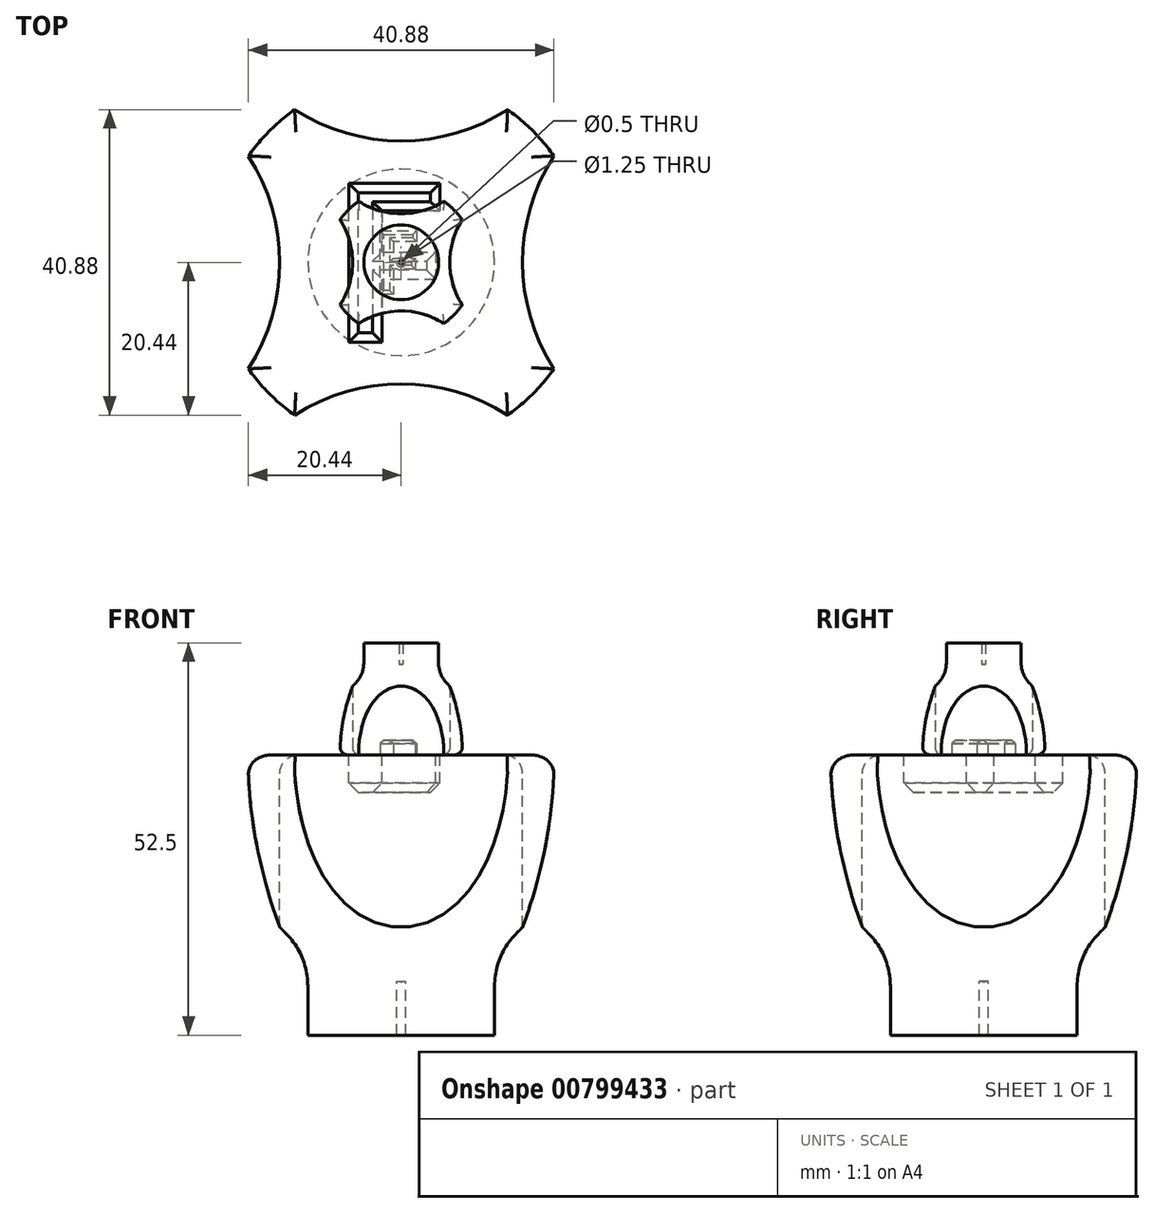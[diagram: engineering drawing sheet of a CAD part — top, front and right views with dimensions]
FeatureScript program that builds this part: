
annotation { "Feature Type Name" : "Feature", "Feature Type Description" : "" }
export const myFeature = defineFeature(function(context is Context, id is Id, definition is map)
    precondition{}
    {
        {
            var Q0;
            Q0=qCreatedBy(makeId("Top.planeOp"),FACE);
            var sketch = newSketch(context, id + "F0", { "sketchPlane" : qUnion([Q0])});
            skCircle(sketch, "E0", {"center": v(0, 0) * mm, "radius": 10 * mm});
            skCircle(sketch, "E1", {"center": v(0, 17) * mm, "radius": 10.5 * mm});
            skCircle(sketch, "E2.1.0", {"center": v(-17, 0) * mm, "radius": 10.5 * mm});
            skCircle(sketch, "E2.2.0", {"center": v(0, -17) * mm, "radius": 10.5 * mm});
            skCircle(sketch, "E2.3.0", {"center": v(17, 0) * mm, "radius": 10.5 * mm});
            skSolve(sketch);
        }
        {
            var Q0;
            Q0=qCreatedBy(makeId("Front.planeOp"),FACE);
            var Q1;
            Q1=qCreatedBy(makeId("Front.planeOp"),FACE);
            var sketch = newSketch(context, id + "F1", { "sketchPlane" : qUnion([Q0, Q1])});
            skLineSegment(sketch, "E3.0", {"start": v(-10, 0) * mm, "end": v(0, 0) * mm});
            skEllipticalArc(sketch, "E4", {});
            skLineSegment(sketch, "E5", {"start": v(0, -5.12) * mm, "end": v(0, 66.05) * mm, "construction": true});
            skLineSegment(sketch, "E6", {"start": v(0, 0) * mm, "end": v(0, 12.13) * mm});
            skPoint(sketch, "E7.orphan", {"position": v(10, 0) * mm});
            const initialGuessF1  = {"E4": [0, 0, -1, 0, 0.01, 0.012128176619593395, 4.71238898038469, 6.283185307179586]};
            skSetInitialGuess(sketch, initialGuessF1);
            skSolve(sketch);
        }
        {
            var Q0;
            Q0=makeQuery(id+"F1.imprint","IMPRINT",FACE,{"disambiguationData":[TD([[makeQuery(id+"F1.imprint","IMPRINT",EDGE,{"derivedFrom":sQuery(id+"F1.wireOp",EDGE,"E4")}),1.0]])]});
            var Q1;
            Q1=sQuery(id+"F1.wireOp",EDGE,"E5");
            revolve(context, id + "F2", {"surfaceOperationType" : NewSurfaceOperationType.NEW, "entities" : qUnion([Q0]), "axis" : qUnion([Q1]), "revolveType" : RevolveType.FULL});
        }
        {
            var Q0;
            {var subQ0=sQuery(id+"F0.wireOp",EDGE,"E2.1.0");var subQ1=sQuery(id+"F0.wireOp",EDGE,"E0");var subQ2=makeQuery(id+"F0.imprint","INTERSECT",VERTEX,{"disambiguationData":[OD(0.0)],"derivedFrom":[subQ1,subQ0]});Q0=makeQuery(id+"F0.imprint","IMPRINT",FACE,{"disambiguationData":[TD([[makeQuery(id+"F0.imprint","IMPRINT",EDGE,{"disambiguationData":[TD([[subQ2,-1.0]])],"derivedFrom":subQ1}),1.0]])]});}
            var Q1;
            {var subQ0=sQuery(id+"F0.wireOp",EDGE,"E2.2.0");var subQ1=sQuery(id+"F0.wireOp",EDGE,"E0");var subQ2=makeQuery(id+"F0.imprint","INTERSECT",VERTEX,{"disambiguationData":[OD(0.0)],"derivedFrom":[subQ1,subQ0]});Q1=makeQuery(id+"F0.imprint","IMPRINT",FACE,{"disambiguationData":[TD([[makeQuery(id+"F0.imprint","IMPRINT",EDGE,{"disambiguationData":[TD([[subQ2,-1.0]])],"derivedFrom":subQ1}),1.0]])]});}
            var Q2;
            {var subQ0=sQuery(id+"F0.wireOp",EDGE,"E2.3.0");var subQ1=sQuery(id+"F0.wireOp",EDGE,"E0");var subQ2=makeQuery(id+"F0.imprint","INTERSECT",VERTEX,{"disambiguationData":[OD(0.0)],"derivedFrom":[subQ1,subQ0]});Q2=makeQuery(id+"F0.imprint","IMPRINT",FACE,{"disambiguationData":[TD([[makeQuery(id+"F0.imprint","IMPRINT",EDGE,{"disambiguationData":[TD([[subQ2,1.0]])],"derivedFrom":subQ1}),1.0]])]});}
            var Q3;
            {var subQ0=sQuery(id+"F0.wireOp",EDGE,"E1");var subQ1=sQuery(id+"F0.wireOp",EDGE,"E0");var subQ2=makeQuery(id+"F0.imprint","INTERSECT",VERTEX,{"disambiguationData":[OD(0.0)],"derivedFrom":[subQ1,subQ0]});Q3=makeQuery(id+"F0.imprint","IMPRINT",FACE,{"disambiguationData":[TD([[makeQuery(id+"F0.imprint","IMPRINT",EDGE,{"disambiguationData":[TD([[subQ2,-1.0]])],"derivedFrom":subQ1}),1.0]])]});}
            var Q4;
            Q4=makeQuery(id+"F2.opRevolve","SWEPT_FACE",FACE,{"disambiguationData":[OSD([sQuery(id+"F1.wireOp",EDGE,"E4")])]});
            extrude(context, id + "F3", {"entities" : qUnion([Q0, Q1, Q2, Q3]), "operationType" : NewBodyOperationType.REMOVE, "endBound" : BoundingType.UP_TO_SURFACE, "depth" : 25 * mm, "endBoundEntityFace" : qUnion([Q4]), "offsetDistance" : 25 * mm});
        }
        {
            var Q0;
            Q0=qCreatedBy(makeId("Top.planeOp"),FACE);
            var sketch = newSketch(context, id + "F4", { "sketchPlane" : qUnion([Q0])});
            skCircle(sketch, "E8.cCircle", {"center": v(0, 0) * mm, "radius": 4 * mm, "construction": true});
            skLineSegment(sketch, "E8.0", {"start": v(2.3, -4) * mm, "end": v(-2.3, -4) * mm});
            skLineSegment(sketch, "E8.1", {"start": v(-2.3, -4) * mm, "end": v(-4.62, 0) * mm});
            skLineSegment(sketch, "E8.2", {"start": v(-4.62, 0) * mm, "end": v(-2.3, 4) * mm});
            skLineSegment(sketch, "E8.3", {"start": v(-2.3, 4) * mm, "end": v(2.3, 4) * mm});
            skLineSegment(sketch, "E8.4", {"start": v(2.3, 4) * mm, "end": v(4.62, 0) * mm});
            skLineSegment(sketch, "E8.5", {"start": v(4.62, 0) * mm, "end": v(2.3, -4) * mm});
            skPoint(sketch, "E8.0.midPoint", {"position": v(0, -4) * mm});
            skSolve(sketch);
        }
        {
            var Q0;
            Q0=makeQuery(id+"F3.boolean.opBoolean","COPY",EDGE,{"derivedFrom":makeQuery(id+"F3.opExtrude","CAP_EDGE",EDGE,{"disambiguationData":[OSD([sQuery(id+"F0.wireOp",EDGE,"E2.2.0")])],"isStart":false})});
            var Q1;
            Q1=makeQuery(id+"F3.boolean.opBoolean","COPY",EDGE,{"derivedFrom":makeQuery(id+"F3.opExtrude","CAP_EDGE",EDGE,{"disambiguationData":[OSD([sQuery(id+"F0.wireOp",EDGE,"E2.1.0")])],"isStart":false})});
            var Q2;
            Q2=makeQuery(id+"F2.opRevolve","SWEPT_FACE",FACE,{"disambiguationData":[OSD([sQuery(id+"F1.wireOp",EDGE,"E3.0")])]});
            var Q3;
            Q3=makeQuery(id+"F3.boolean.opBoolean","COPY",EDGE,{"derivedFrom":makeQuery(id+"F3.opExtrude","CAP_EDGE",EDGE,{"disambiguationData":[OSD([sQuery(id+"F0.wireOp",EDGE,"E1")])],"isStart":false})});
            var Q4;
            Q4=makeQuery(id+"F3.boolean.opBoolean","COPY",EDGE,{"derivedFrom":makeQuery(id+"F3.opExtrude","CAP_EDGE",EDGE,{"disambiguationData":[OSD([sQuery(id+"F0.wireOp",EDGE,"E2.3.0")])],"isStart":false})});
            fillet(context, id + "F5", {"entities" : qUnion([Q0, Q1, Q2, Q3, Q4]), "radius" : 1 * mm, "tangentPropagation" : true, "allowEdgeOverflow" : false});
        }
        {
            var Q0;
            Q0=qCreatedBy(makeId("Top.planeOp"),FACE);
            var sketch = newSketch(context, id + "F6", { "sketchPlane" : qUnion([Q0])});
            skCircle(sketch, "E9", {"center": v(0, 0) * mm, "radius": 5 * mm});
            skCircle(sketch, "E10", {"center": v(0, 0) * mm, "radius": 0.25 * mm});
            skSolve(sketch);
        }
        {
            var Q0;
            Q0=makeQuery(id+"F6.imprint","IMPRINT",FACE,{"disambiguationData":[TD([[makeQuery(id+"F6.imprint","IMPRINT",EDGE,{"derivedFrom":sQuery(id+"F6.wireOp",EDGE,"E9")}),1.0]])]});
            extrude(context, id + "F7", {"entities" : qUnion([Q0]), "operationType" : NewBodyOperationType.ADD, "depth" : 15 * mm, "offsetDistance" : 25 * mm});
        }
        {
            var Q0;
            Q0=makeQuery(id+"F7.boolean.opBoolean","INTERSECT",EDGE,{"derivedFrom":[makeQuery(id+"F2.opRevolve","SWEPT_FACE",FACE,{"disambiguationData":[OSD([sQuery(id+"F1.wireOp",EDGE,"E4")])]}),makeQuery(id+"F7.opExtrude","SWEPT_FACE",FACE,{"disambiguationData":[OSD([sQuery(id+"F6.wireOp",EDGE,"E9")])]})]});
            fillet(context, id + "F8", {"entities" : qUnion([Q0]), "radius" : 4 * mm, "tangentPropagation" : true, "allowEdgeOverflow" : false});
        }
        {
            var Q0;
            Q0=qCreatedBy(makeId("Top.planeOp"),FACE);
            var sketch = newSketch(context, id + "F9", { "sketchPlane" : qUnion([Q0])});
            skText(sketch, "E11", { "text": "F", "fontName": "OpenSans-Bold.ttf"});
            const initialGuessF9  = {"E11": [-0.00387, -0.00427, 1, 0, 0.00857]};
            skSetInitialGuess(sketch, initialGuessF9);
            skSolve(sketch);
        }
        {
            var Q0;
            Q0=makeQuery(id+"F9.imprint","IMPRINT",FACE,{"disambiguationData":[TD([[makeQuery(id+"F9.imprint","IMPRINT",EDGE,{"derivedFrom":sQuery(id+"F9.wireOp",EDGE,"E11.sketch_text.stroke-0")}),-1.0]])]});
            extrude(context, id + "F10", {"entities" : qUnion([Q0]), "operationType" : NewBodyOperationType.REMOVE, "depth" : 2 * mm, "offsetDistance" : 25 * mm});
        }
        {
            var Q0;
            Q0=makeQuery(id+"F10.boolean.opBoolean","COPY",FACE,{"derivedFrom":makeQuery(id+"F10.opExtrude","CAP_FACE",FACE,{"disambiguationData":[OSD([sQuery(id+"F9.wireOp",EDGE,"E11.sketch_text.stroke-0"),sQuery(id+"F9.wireOp",EDGE,"E11.sketch_text.stroke-1"),sQuery(id+"F9.wireOp",EDGE,"E11.sketch_text.stroke-2"),sQuery(id+"F9.wireOp",EDGE,"E11.sketch_text.stroke-3"),sQuery(id+"F9.wireOp",EDGE,"E11.sketch_text.stroke-4"),sQuery(id+"F9.wireOp",EDGE,"E11.sketch_text.stroke-5"),sQuery(id+"F9.wireOp",EDGE,"E11.sketch_text.stroke-6"),sQuery(id+"F9.wireOp",EDGE,"E11.sketch_text.stroke-7"),sQuery(id+"F9.wireOp",EDGE,"E11.sketch_text.stroke-8"),sQuery(id+"F9.wireOp",EDGE,"E11.sketch_text.stroke-9")])],"isStart":false})});
            var Q1;
            Q1=makeQuery(id+"F10.boolean.opBoolean","COPY",EDGE,{"derivedFrom":makeQuery(id+"F10.opExtrude","CAP_EDGE",EDGE,{"disambiguationData":[OSD([sQuery(id+"F9.wireOp",EDGE,"E11.sketch_text.stroke-9")])],"isStart":true})});
            var Q2;
            Q2=makeQuery(id+"F10.boolean.opBoolean","COPY",EDGE,{"derivedFrom":makeQuery(id+"F10.opExtrude","CAP_EDGE",EDGE,{"disambiguationData":[OSD([sQuery(id+"F9.wireOp",EDGE,"E11.sketch_text.stroke-8")])],"isStart":true})});
            var Q3;
            Q3=makeQuery(id+"F10.boolean.opBoolean","COPY",EDGE,{"derivedFrom":makeQuery(id+"F10.opExtrude","CAP_EDGE",EDGE,{"disambiguationData":[OSD([sQuery(id+"F9.wireOp",EDGE,"E11.sketch_text.stroke-7")])],"isStart":true})});
            var Q4;
            Q4=makeQuery(id+"F10.boolean.opBoolean","COPY",EDGE,{"derivedFrom":makeQuery(id+"F10.opExtrude","CAP_EDGE",EDGE,{"disambiguationData":[OSD([sQuery(id+"F9.wireOp",EDGE,"E11.sketch_text.stroke-6")])],"isStart":true})});
            var Q5;
            Q5=makeQuery(id+"F10.boolean.opBoolean","COPY",EDGE,{"derivedFrom":makeQuery(id+"F10.opExtrude","CAP_EDGE",EDGE,{"disambiguationData":[OSD([sQuery(id+"F9.wireOp",EDGE,"E11.sketch_text.stroke-5")])],"isStart":true})});
            var Q6;
            Q6=makeQuery(id+"F10.boolean.opBoolean","COPY",EDGE,{"derivedFrom":makeQuery(id+"F10.opExtrude","CAP_EDGE",EDGE,{"disambiguationData":[OSD([sQuery(id+"F9.wireOp",EDGE,"E11.sketch_text.stroke-4")])],"isStart":true})});
            var Q7;
            Q7=makeQuery(id+"F10.boolean.opBoolean","COPY",EDGE,{"derivedFrom":makeQuery(id+"F10.opExtrude","CAP_EDGE",EDGE,{"disambiguationData":[OSD([sQuery(id+"F9.wireOp",EDGE,"E11.sketch_text.stroke-3")])],"isStart":true})});
            var Q8;
            Q8=makeQuery(id+"F10.boolean.opBoolean","COPY",EDGE,{"derivedFrom":makeQuery(id+"F10.opExtrude","CAP_EDGE",EDGE,{"disambiguationData":[OSD([sQuery(id+"F9.wireOp",EDGE,"E11.sketch_text.stroke-2")])],"isStart":true})});
            var Q9;
            Q9=makeQuery(id+"F10.boolean.opBoolean","COPY",EDGE,{"derivedFrom":makeQuery(id+"F10.opExtrude","CAP_EDGE",EDGE,{"disambiguationData":[OSD([sQuery(id+"F9.wireOp",EDGE,"E11.sketch_text.stroke-1")])],"isStart":true})});
            var Q10;
            Q10=makeQuery(id+"F10.boolean.opBoolean","COPY",EDGE,{"derivedFrom":makeQuery(id+"F10.opExtrude","CAP_EDGE",EDGE,{"disambiguationData":[OSD([sQuery(id+"F9.wireOp",EDGE,"E11.sketch_text.stroke-0")])],"isStart":true})});
            chamfer(context, id + "F11", {"entities" : qUnion([Q0, Q1, Q2, Q3, Q4, Q5, Q6, Q7, Q8, Q9, Q10]), "width" : 0.5 * mm, "tangentPropagation" : true});
        }
        {
            var Q0;
            Q0=makeQuery(id+"F2.opRevolve","SWEPT_BODY",BODY,{"disambiguationData":[OSD([sQuery(id+"F1.wireOp",EDGE,"E4"),sQuery(id+"F1.wireOp",EDGE,"E3.0"),sQuery(id+"F1.wireOp",EDGE,"E6")])]});
            var Q1;
            Q1=qCreatedBy(makeId("Top.planeOp"),FACE);
            mirror(context, id + "F12", {"entities" : qUnion([Q0]), "mirrorPlane" : qUnion([Q1])});
        }
        {
            var Q0;
            Q0=makeQuery(id+"F12.opPattern","COPY",BODY,{"derivedFrom":makeQuery(id+"F2.opRevolve","SWEPT_BODY",BODY,{"disambiguationData":[OSD([sQuery(id+"F1.wireOp",EDGE,"E4"),sQuery(id+"F1.wireOp",EDGE,"E3.0"),sQuery(id+"F1.wireOp",EDGE,"E6")])]}),"instanceName":"1"});
            var Q1;
            Q1=sQuery(id+"F4.wireOp",VERTEX,"E8.cCircle.center");
            transform(context, id + "F13", {"entities" : qUnion([Q0]), "transformType" : TransformType.SCALE_UNIFORMLY, "scale" : 2.5, "scalePoint" : qUnion([Q1]), "makeCopy" : false});
        }
    });
